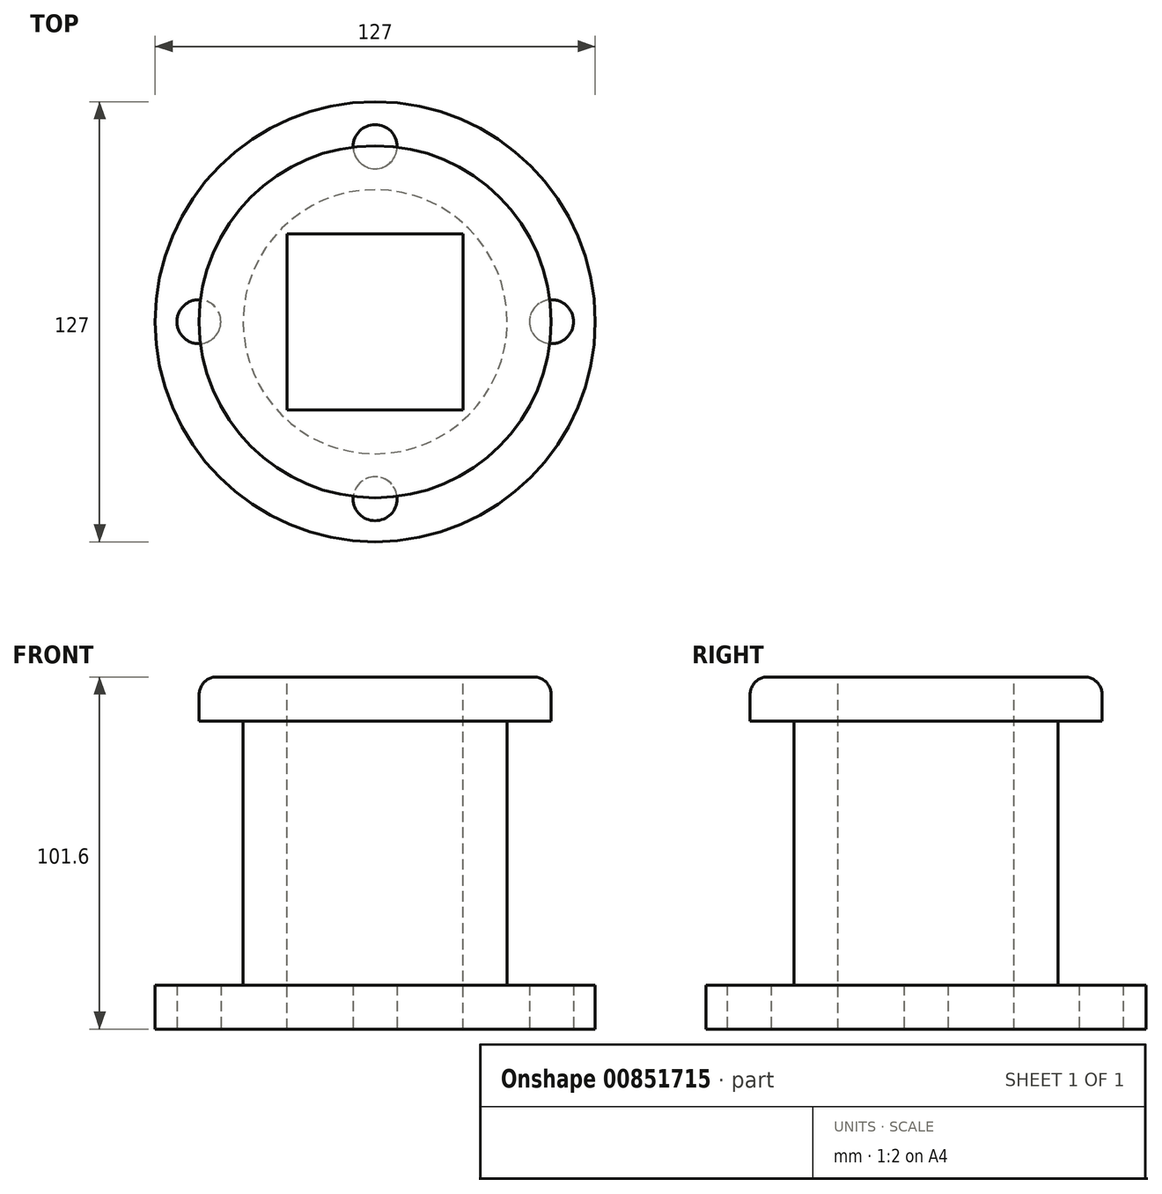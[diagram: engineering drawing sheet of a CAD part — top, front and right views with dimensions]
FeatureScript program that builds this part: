
annotation { "Feature Type Name" : "Feature", "Feature Type Description" : "" }
export const myFeature = defineFeature(function(context is Context, id is Id, definition is map)
    precondition{}
    {
        {
            var Q0;
            Q0=qCreatedBy(makeId("Top.planeOp"),FACE);
            var sketch = newSketch(context, id + "F0", { "sketchPlane" : qUnion([Q0])});
            skCircle(sketch, "E0", {"center": v(0, 0) * mm, "radius": 63.5 * mm});
            skSolve(sketch);
        }
        {
            var Q0;
            Q0 = qSketchRegion(id + "F0", true);
            extrude(context, id + "F1", {"entities" : qUnion([Q0]), "depth" : 12.7 * mm, "offsetDistance" : 25.4 * mm});
        }
        {
            var Q0;
            Q0=makeQuery(id+"F1.opExtrude","CAP_FACE",FACE,{"disambiguationData":[OSD([sQuery(id+"F0.wireOp",EDGE,"E0")])],"isStart":false});
            var sketch = newSketch(context, id + "F2", { "sketchPlane" : qUnion([Q0])});
            skCircle(sketch, "E1", {"center": v(0, 0) * mm, "radius": 31.75 * mm});
            skSolve(sketch);
        }
        {
            var Q0;
            Q0 = qSketchRegion(id + "F2", true);
            extrude(context, id + "F3", {"entities" : qUnion([Q0]), "operationType" : NewBodyOperationType.REMOVE, "depth" : 76.2 * mm, "offsetDistance" : 25.4 * mm});
        }
        {
            var Q0;
            Q0=makeQuery(id+"F1.opExtrude","CAP_FACE",FACE,{"disambiguationData":[OSD([sQuery(id+"F0.wireOp",EDGE,"E0")])],"isStart":false});
            var sketch = newSketch(context, id + "F4", { "sketchPlane" : qUnion([Q0])});
            skCircle(sketch, "E2", {"center": v(0, 0) * mm, "radius": 38.1 * mm});
            skSolve(sketch);
        }
        {
            var Q0;
            Q0 = qSketchRegion(id + "F4", true);
            extrude(context, id + "F5", {"entities" : qUnion([Q0]), "operationType" : NewBodyOperationType.ADD, "depth" : 76.2 * mm, "offsetDistance" : 25.4 * mm});
        }
        {
            var Q0;
            Q0=makeQuery(id+"F5.opExtrude","CAP_FACE",FACE,{"disambiguationData":[OSD([sQuery(id+"F4.wireOp",EDGE,"E2")])],"isStart":false});
            var sketch = newSketch(context, id + "F6", { "sketchPlane" : qUnion([Q0])});
            skCircle(sketch, "E3", {"center": v(0, 0) * mm, "radius": 50.8 * mm});
            skSolve(sketch);
        }
        {
            var Q0;
            Q0 = qSketchRegion(id + "F6", true);
            extrude(context, id + "F7", {"entities" : qUnion([Q0]), "operationType" : NewBodyOperationType.ADD, "depth" : 12.7 * mm, "offsetDistance" : 25.4 * mm});
        }
        {
            var Q0;
            Q0=makeQuery(id+"F7.opExtrude","CAP_EDGE",EDGE,{"disambiguationData":[OSD([sQuery(id+"F6.wireOp",EDGE,"E3")])],"isStart":false});
            fillet(context, id + "F8", {"entities" : qUnion([Q0]), "radius" : 5.08 * mm, "tangentPropagation" : true, "allowEdgeOverflow" : false});
        }
        {
            var Q0;
            Q0=makeQuery(id+"F1.opExtrude","CAP_FACE",FACE,{"disambiguationData":[OSD([sQuery(id+"F0.wireOp",EDGE,"E0")])],"isStart":true});
            var sketch = newSketch(context, id + "F9", { "sketchPlane" : qUnion([Q0])});
            skLineSegment(sketch, "E4", {"start": v(0, 0) * mm, "end": v(50.89, 0) * mm});
            skLineSegment(sketch, "E5", {"start": v(50.89, 0) * mm, "end": v(0, 0) * mm});
            skLineSegment(sketch, "E6", {"start": v(0, -50.5) * mm, "end": v(0, 0) * mm});
            skLineSegment(sketch, "E7", {"start": v(-50.89, 0) * mm, "end": v(0, 0) * mm});
            skLineSegment(sketch, "E8", {"start": v(0, 51.08) * mm, "end": v(0, 0) * mm});
            skCircle(sketch, "E9", {"center": v(0, 51.08) * mm, "radius": 6.35 * mm});
            skCircle(sketch, "E10", {"center": v(50.89, 0) * mm, "radius": 6.35 * mm});
            skCircle(sketch, "E11", {"center": v(0, -50.5) * mm, "radius": 6.35 * mm});
            skCircle(sketch, "E12", {"center": v(-50.89, 0) * mm, "radius": 6.35 * mm});
            skSolve(sketch);
        }
        {
            var Q0;
            Q0 = qSketchRegion(id + "F9", true);
            extrude(context, id + "F10", {"entities" : qUnion([Q0]), "operationType" : NewBodyOperationType.REMOVE, "oppositeDirection" : true, "depth" : 50.8 * mm, "offsetDistance" : 25.4 * mm});
        }
        {
            var Q0;
            Q0=makeQuery(id+"F7.opExtrude","CAP_FACE",FACE,{"disambiguationData":[OSD([sQuery(id+"F6.wireOp",EDGE,"E3")])],"isStart":false});
            var sketch = newSketch(context, id + "F11", { "sketchPlane" : qUnion([Q0])});
            skLineSegment(sketch, "E13.bottom", {"start": v(25.4, -25.4) * mm, "end": v(-25.4, -25.4) * mm});
            skLineSegment(sketch, "E13.top", {"start": v(25.4, 25.4) * mm, "end": v(-25.4, 25.4) * mm});
            skLineSegment(sketch, "E13.left", {"start": v(25.4, -25.4) * mm, "end": v(25.4, 25.4) * mm});
            skLineSegment(sketch, "E13.right", {"start": v(-25.4, -25.4) * mm, "end": v(-25.4, 25.4) * mm});
            skPoint(sketch, "E13.middle", {"position": v(0, 0) * mm});
            skSolve(sketch);
        }
        {
            var Q0;
            Q0 = qSketchRegion(id + "F11", true);
            extrude(context, id + "F12", {"entities" : qUnion([Q0]), "operationType" : NewBodyOperationType.REMOVE, "oppositeDirection" : true, "depth" : 120.14 * mm, "offsetDistance" : 25.4 * mm});
        }
    });
